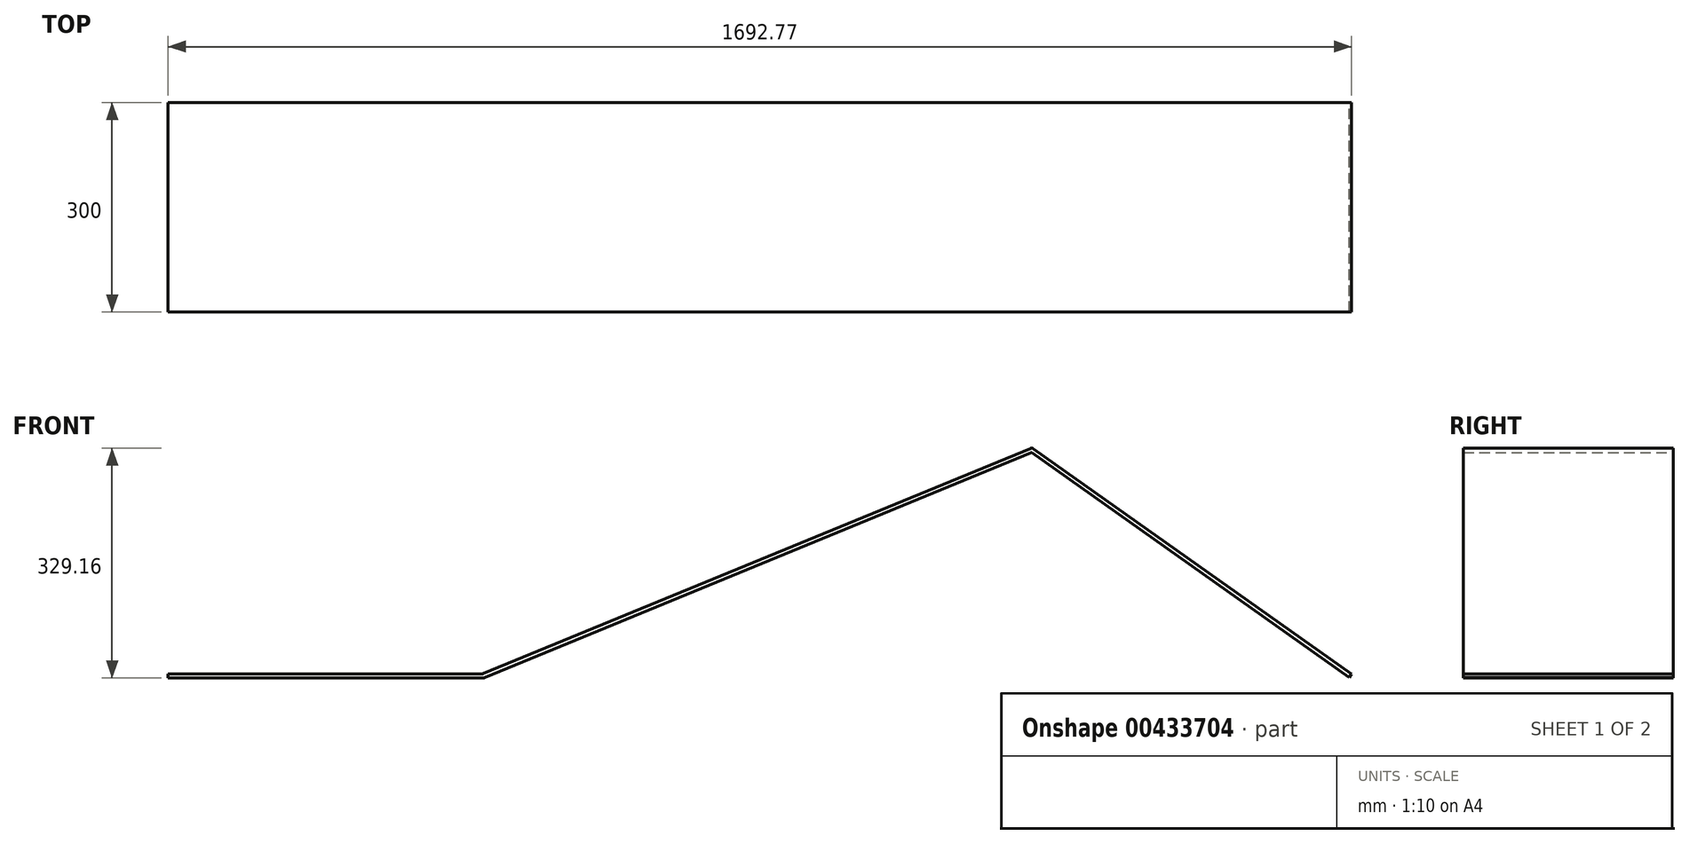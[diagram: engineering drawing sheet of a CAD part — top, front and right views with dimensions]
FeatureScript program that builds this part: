
annotation { "Feature Type Name" : "Feature", "Feature Type Description" : "" }
export const myFeature = defineFeature(function(context is Context, id is Id, definition is map)
    precondition{}
    {
        {
            var Q0;
            Q0=qCreatedBy(makeId("Front.planeOp"),FACE);
            var sketch = newSketch(context, id + "F0", { "sketchPlane" : qUnion([Q0])});
            skLineSegment(sketch, "E0", {"start": v(0, 0) * mm, "end": v(449.01, 0) * mm});
            skLineSegment(sketch, "E1", {"start": v(450.92, 0.38) * mm, "end": v(1233.35, 322.78) * mm});
            skLineSegment(sketch, "E2", {"start": v(1238.14, 322.24) * mm, "end": v(1692.77, 0) * mm});
            skPoint(sketch, "E3.visualSharp", {"position": v(450, 0) * mm});
            skArc(sketch, "E3.filletArc", {"start": v(449.01, 0) * mm, "mid": v(449.98, 0.1) * mm, "end": v(450.92, 0.38) * mm});
            skPoint(sketch, "E4.visualSharp", {"position": v(1235.9, 323.83) * mm});
            skArc(sketch, "E4.filletArc", {"start": v(1238.14, 322.24) * mm, "mid": v(1235.82, 323.13) * mm, "end": v(1233.35, 322.78) * mm});
            skLineSegment(sketch, "E5.0", {"start": v(0, -6) * mm, "end": v(449.01, -6) * mm});
            skLineSegment(sketch, "E6.0", {"start": v(1235.57, 316.7) * mm, "end": v(1689.3, -4.9) * mm});
            skLineSegment(sketch, "E7", {"start": v(1692.77, 0) * mm, "end": v(1689.3, -4.9) * mm});
            skLineSegment(sketch, "E8", {"start": v(0, 0) * mm, "end": v(0, -6) * mm});
            skLineSegment(sketch, "E9.0", {"start": v(453.2, -5.17) * mm, "end": v(1234.61, 316.82) * mm});
            skArc(sketch, "E10.0", {"start": v(449.01, -6) * mm, "mid": v(451.15, -5.8) * mm, "end": v(453.2, -5.17) * mm});
            skArc(sketch, "E11.filletArc", {"start": v(1235.57, 316.7) * mm, "mid": v(1235.1, 316.89) * mm, "end": v(1234.61, 316.82) * mm});
            skSolve(sketch);
        }
        {
            var Q0;
            Q0=makeQuery(id+"F0.imprint","IMPRINT",FACE,{"disambiguationData":[TD([[makeQuery(id+"F0.imprint","IMPRINT",EDGE,{"derivedFrom":sQuery(id+"F0.wireOp",EDGE,"E0")}),-1.0]])]});
            extrude(context, id + "F1", {"entities" : qUnion([Q0]), "depth" : 300 * mm});
        }
    });
